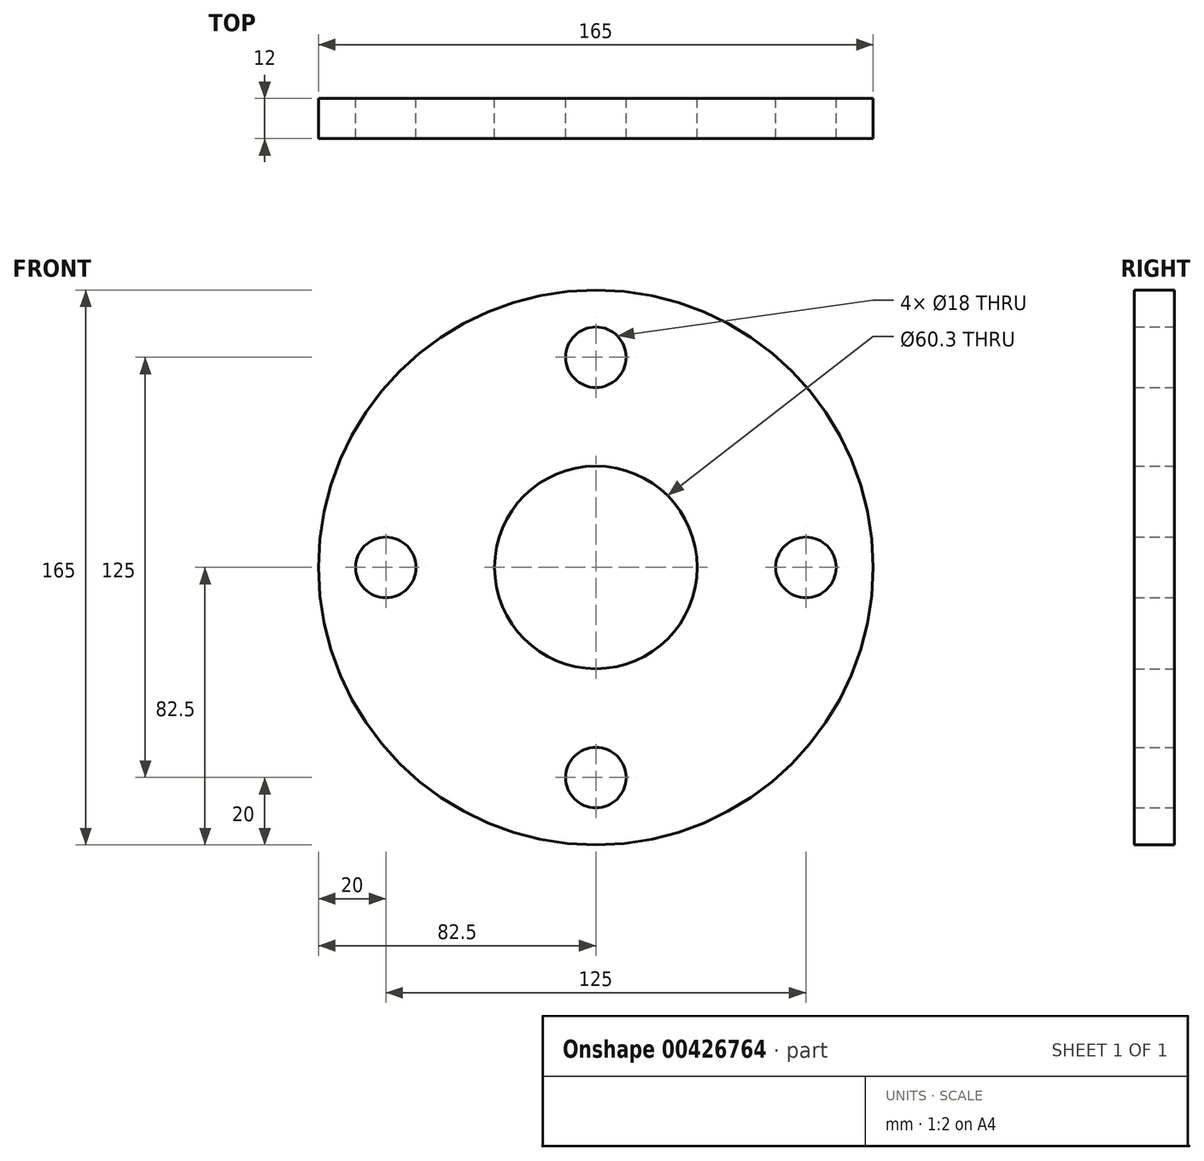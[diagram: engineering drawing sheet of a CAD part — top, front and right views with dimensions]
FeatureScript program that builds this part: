
annotation { "Feature Type Name" : "Feature", "Feature Type Description" : "" }
export const myFeature = defineFeature(function(context is Context, id is Id, definition is map)
    precondition{}
    {
        {
            var Q0;
            Q0=qCreatedBy(makeId("Front.planeOp"),FACE);
            var sketch = newSketch(context, id + "F0", { "sketchPlane" : qUnion([Q0])});
            skCircle(sketch, "E0", {"center": v(0, 0) * mm, "radius": 82.5 * mm});
            skCircle(sketch, "E1", {"center": v(0, 0) * mm, "radius": 30.15 * mm});
            skCircle(sketch, "E2", {"center": v(0, 0) * mm, "radius": 62.5 * mm, "construction": true});
            skCircle(sketch, "E3", {"center": v(0, 62.5) * mm, "radius": 9 * mm});
            skCircle(sketch, "E4.1.0", {"center": v(-62.5, 0) * mm, "radius": 9 * mm});
            skCircle(sketch, "E4.2.0", {"center": v(0, -62.5) * mm, "radius": 9 * mm});
            skCircle(sketch, "E5.1.3.0", {"center": v(62.5, 0) * mm, "radius": 9 * mm});
            skSolve(sketch);
        }
        {
            var Q0;
            Q0=makeQuery(id+"F0.imprint","IMPRINT",FACE,{"disambiguationData":[TD([[makeQuery(id+"F0.imprint","IMPRINT",EDGE,{"derivedFrom":sQuery(id+"F0.wireOp",EDGE,"E0")}),1.0]])]});
            extrude(context, id + "F1", {"entities" : qUnion([Q0]), "depth" : 12 * mm});
        }
    });
